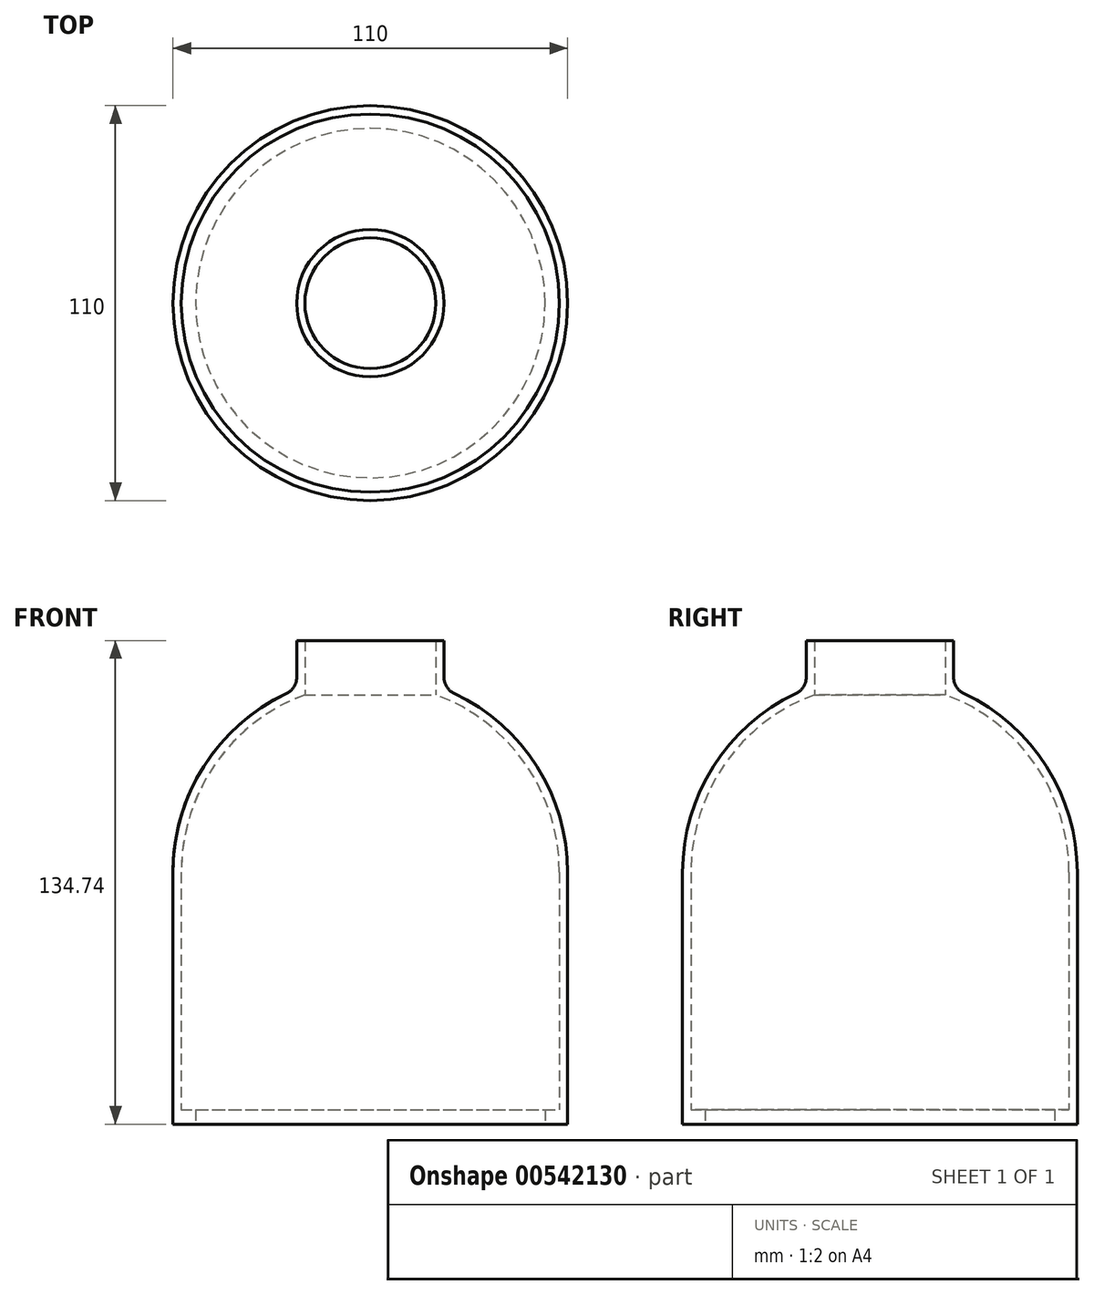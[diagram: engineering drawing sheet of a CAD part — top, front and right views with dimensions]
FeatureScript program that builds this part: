
annotation { "Feature Type Name" : "Feature", "Feature Type Description" : "" }
export const myFeature = defineFeature(function(context is Context, id is Id, definition is map)
    precondition{}
    {
        {
            var Q0;
            Q0=qCreatedBy(makeId("Front.planeOp"),FACE);
            var sketch = newSketch(context, id + "F0", { "sketchPlane" : qUnion([Q0])});
            skLineSegment(sketch, "E0.bottom", {"start": v(-55, 55) * mm, "end": v(55, 55) * mm, "construction": true});
            skLineSegment(sketch, "E0.top", {"start": v(-55, -55) * mm, "end": v(55, -55) * mm, "construction": true});
            skLineSegment(sketch, "E0.left", {"start": v(-55, 55) * mm, "end": v(-55, -55) * mm, "construction": true});
            skLineSegment(sketch, "E0.right", {"start": v(55, 55) * mm, "end": v(55, -55) * mm, "construction": true});
            skPoint(sketch, "E0.middle", {"position": v(0, 0) * mm});
            skLineSegment(sketch, "E1", {"start": v(0, 83.4) * mm, "end": v(0, 12.35) * mm, "construction": true});
            skArc(sketch, "E2", {"start": v(-55, 0) * mm, "mid": v(-46.43, 29.48) * mm, "end": v(-23.4, 49.78) * mm});
            skArc(sketch, "E3.0", {"start": v(-52.7, 0) * mm, "mid": v(-43.24, 30.13) * mm, "end": v(-18.25, 49.44) * mm});
            skLineSegment(sketch, "E4.0", {"start": v(-18.25, 83.4) * mm, "end": v(-18.25, 12.35) * mm, "construction": true});
            skLineSegment(sketch, "E5", {"start": v(-18.25, 49.44) * mm, "end": v(-18.25, 64.55) * mm, "construction": true});
            skLineSegment(sketch, "E6", {"start": v(-18.25, 64.55) * mm, "end": v(-18.25, 49.44) * mm});
            skLineSegment(sketch, "E7", {"start": v(-18.25, 64.55) * mm, "end": v(-20.52, 64.55) * mm});
            skLineSegment(sketch, "E8", {"start": v(-20.52, 64.55) * mm, "end": v(-20.52, 54.3) * mm});
            skArc(sketch, "E9.filletArc", {"start": v(-23.4, 49.78) * mm, "mid": v(-21.3, 51.62) * mm, "end": v(-20.52, 54.3) * mm});
            skLineSegment(sketch, "E10", {"start": v(-55, 0) * mm, "end": v(-55, -70.19) * mm});
            skLineSegment(sketch, "E11", {"start": v(-52.7, 0) * mm, "end": v(-52.7, -66.19) * mm});
            skLineSegment(sketch, "E12", {"start": v(-52.7, -66.19) * mm, "end": v(-48.68, -66.19) * mm});
            skLineSegment(sketch, "E13", {"start": v(-48.68, -66.19) * mm, "end": v(-48.68, -70.19) * mm});
            skLineSegment(sketch, "E14", {"start": v(-48.68, -70.19) * mm, "end": v(-55, -70.19) * mm});
            skSolve(sketch);
        }
        {
            var Q0;
            Q0=sQuery(id+"F0.wireOp",EDGE,"E11");
            var Q1;
            Q1=sQuery(id+"F0.wireOp",EDGE,"E8");
            var Q2;
            Q2=sQuery(id+"F0.wireOp",EDGE,"E3.0");
            var Q3;
            Q3=sQuery(id+"F0.wireOp",EDGE,"E2");
            var Q4;
            Q4=sQuery(id+"F0.wireOp",EDGE,"E10");
            var Q5;
            Q5=sQuery(id+"F0.wireOp",EDGE,"E14");
            var Q6;
            Q6=sQuery(id+"F0.wireOp",EDGE,"E6");
            var Q7;
            Q7=sQuery(id+"F0.wireOp",EDGE,"E9.filletArc");
            var Q8;
            Q8=sQuery(id+"F0.wireOp",EDGE,"E7");
            var Q9;
            Q9=sQuery(id+"F0.wireOp",EDGE,"E13");
            var Q10;
            Q10=sQuery(id+"F0.wireOp",EDGE,"E12");
            var Q11;
            Q11=sQuery(id+"F0.wireOp",EDGE,"E1");
            revolve(context, id + "F1", {"bodyType" : ToolBodyType.SURFACE, "surfaceEntities" : qUnion([Q0, Q1, Q2, Q3, Q4, Q5, Q6, Q7, Q8, Q9, Q10]), "axis" : qUnion([Q11]), "revolveType" : RevolveType.FULL});
        }
    });
